# Revit family: Toilet_Seat_Cover_Dispenser-Bobrick-B-5221
name_source: partatom
category: Specialty Equipment
units: mm (PartAtom-declared; Revit-internal decimal feet)

## family parameters
Cut with Voids When Loaded = No
Host = Face
OmniClass Number = 23.40.20.21
OmniClass Title = Toilet and Bath Specialties
Part Type = Normal
Room Calculation Point = No
Round Connector Dimension = Use Diameter
Shared = Yes

## types (1)
- B-5221
    ADA Compliant = Yes
    Assembly Code = E1090900
    Default Elevation = 18"
    Description = Surface-Mounted Seat Cover Dispenser, Grey ABS Plastic
    Finish = ABS Plastic-Bobrick-High Gloss-Grey
    Height = 11 1/2"
    Installation Type = Surface Mounted
    Length = 2 7/16"
    Manufacturer = Bobrick
    Material = ABS Plastic-Bobrick-High Gloss-Grey
    Model = B-5221
    Mounting Bracket Height = 30"
    Price = Prices may vary. Please consult Manufacturer Representative for most up-to-date price list.
    Product Documentation Link = https://www.bobrick.com
    Product Page URL = https://www.bobrick.com
    Revised Date = 12/02/2024
    URL = http://www.bobrick.com
    Warranty Documentation Link = https://www.bobrick.com
    Width = 16 1/8"

## geometry (parser evidence)
native form markers: Sweep x3
no freeform markers — native parametric forms only
